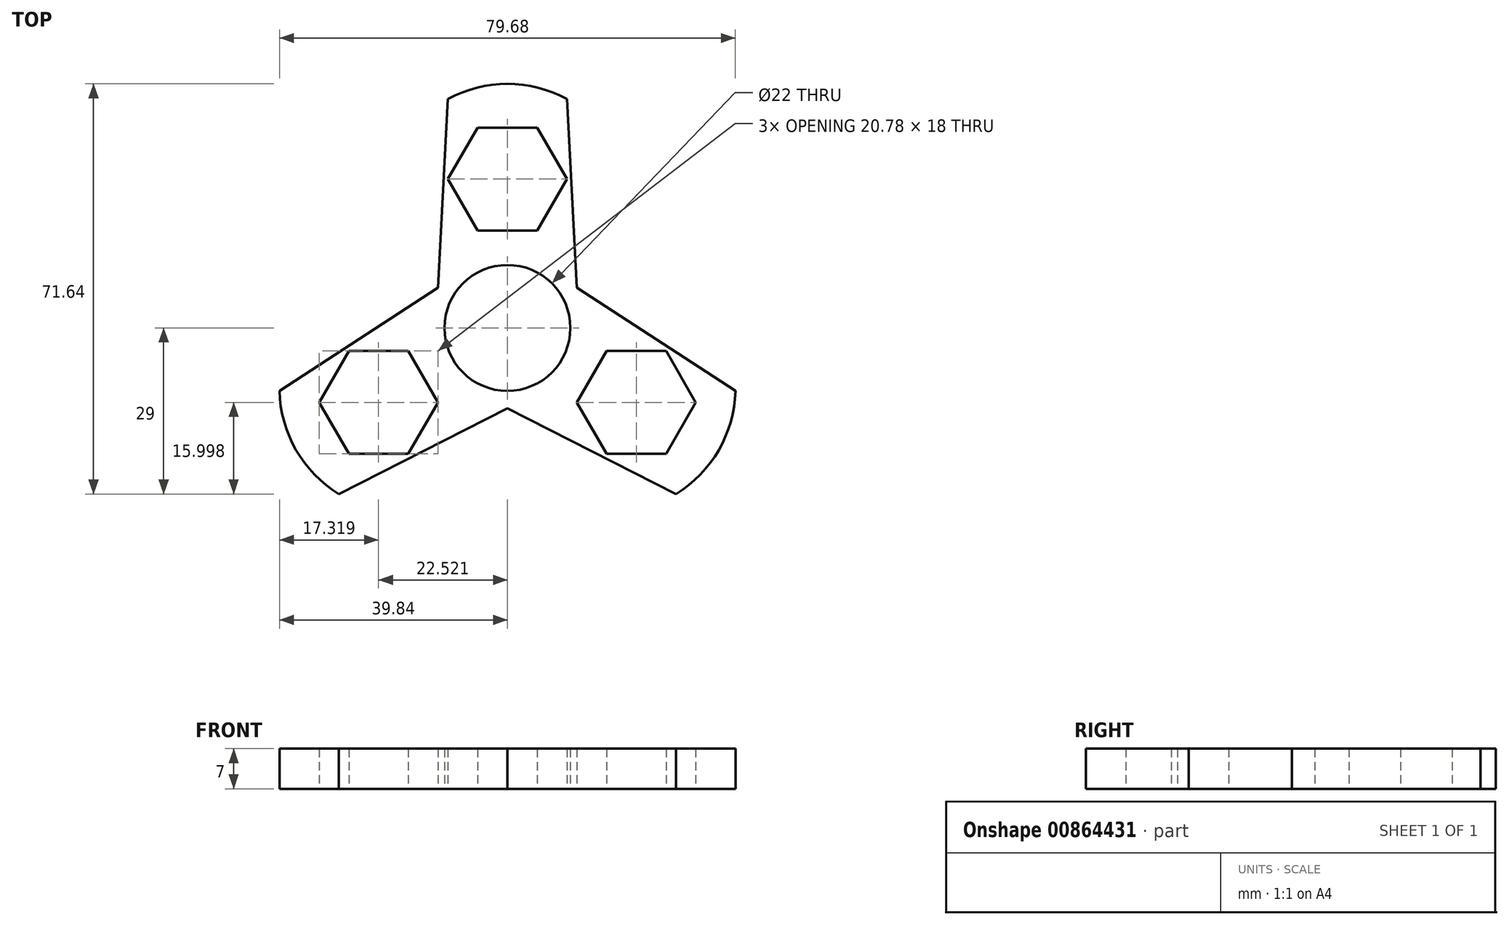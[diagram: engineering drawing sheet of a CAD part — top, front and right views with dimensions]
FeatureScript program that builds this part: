
annotation { "Feature Type Name" : "Feature", "Feature Type Description" : "" }
export const myFeature = defineFeature(function(context is Context, id is Id, definition is map)
    precondition{}
    {
        {
            var Q0;
            Q0=qCreatedBy(makeId("Top.planeOp"),FACE);
            var sketch = newSketch(context, id + "F0", { "sketchPlane" : qUnion([Q0])});
            skCircle(sketch, "E0", {"center": v(0, 0) * mm, "radius": 11 * mm});
            skCircle(sketch, "E1.0", {"center": v(0, 0) * mm, "radius": 14 * mm});
            skCircle(sketch, "E2", {"center": v(0, 0) * mm, "radius": 45 * mm, "construction": true});
            skLineSegment(sketch, "E3", {"start": v(-7.68, 21.31) * mm, "end": v(-7.68, 21.32) * mm});
            skLineSegment(sketch, "E4.MirrorCS", {"start": v(7.68, 21.31) * mm, "end": v(7.68, 21.32) * mm});
            skCircle(sketch, "E5.cCircle", {"center": v(0, 26) * mm, "radius": 9 * mm, "construction": true});
            skPoint(sketch, "E5.cCircle.centerSnap0", {"position": v(6.74, 26) * mm});
            skLineSegment(sketch, "E5.0", {"start": v(-5.2, 35) * mm, "end": v(5.2, 35) * mm});
            skLineSegment(sketch, "E5.1", {"start": v(5.2, 35) * mm, "end": v(10.4, 26) * mm});
            skLineSegment(sketch, "E5.2", {"start": v(10.4, 26) * mm, "end": v(5.2, 17) * mm});
            skLineSegment(sketch, "E5.3", {"start": v(5.2, 17) * mm, "end": v(-5.2, 17) * mm});
            skLineSegment(sketch, "E5.4", {"start": v(-5.2, 17) * mm, "end": v(-10.4, 26) * mm});
            skLineSegment(sketch, "E5.5", {"start": v(-10.4, 26) * mm, "end": v(-5.2, 35) * mm});
            skPoint(sketch, "E5.0.midPoint", {"position": v(0, 35) * mm});
            skLineSegment(sketch, "E6.trimOffspring", {"start": v(-5.28, 33.3) * mm, "end": v(-4.93, 35) * mm});
            skLineSegment(sketch, "E7.trimOffspring", {"start": v(5.28, 33.3) * mm, "end": v(4.93, 35) * mm});
            skPoint(sketch, "E8.start.orphan", {"position": v(-3.48, 42.2) * mm});
            skPoint(sketch, "E9.orphan", {"position": v(-10, 9.8) * mm});
            skPoint(sketch, "E10.orphan", {"position": v(10, 9.8) * mm});
            skPoint(sketch, "E11.orphan", {"position": v(3.48, 42.2) * mm});
            skPoint(sketch, "E12.end.orphan", {"position": v(-10.4, 40) * mm});
            skLineSegment(sketch, "E13", {"start": v(-12.15, 6.96) * mm, "end": v(-10.4, 40) * mm});
            skLineSegment(sketch, "E14.MirrorCS", {"start": v(12.15, 6.96) * mm, "end": v(10.4, 40) * mm});
            skArc(sketch, "E15", {"start": v(10.4, 40) * mm, "mid": v(0, 42.64) * mm, "end": v(-10.4, 40) * mm});
            skCircle(sketch, "E16.1.0", {"center": v(-22.52, -13) * mm, "radius": 9 * mm, "construction": true});
            skArc(sketch, "E16.1.1", {"start": v(-39.84, -11) * mm, "mid": v(-36.93, -21.32) * mm, "end": v(-29.45, -29) * mm});
            skLineSegment(sketch, "E16.1.2", {"start": v(0.04, -14) * mm, "end": v(-29.45, -29) * mm});
            skLineSegment(sketch, "E16.1.3", {"start": v(-12.1, 7.04) * mm, "end": v(-39.84, -11) * mm});
            skLineSegment(sketch, "E16.1.4", {"start": v(-17.32, -22) * mm, "end": v(-27.72, -22) * mm});
            skLineSegment(sketch, "E16.1.5", {"start": v(-12.13, -13) * mm, "end": v(-17.32, -22) * mm});
            skLineSegment(sketch, "E16.1.6", {"start": v(-17.32, -4) * mm, "end": v(-12.13, -13) * mm});
            skLineSegment(sketch, "E16.1.7", {"start": v(-27.72, -4) * mm, "end": v(-17.32, -4) * mm});
            skLineSegment(sketch, "E16.1.8", {"start": v(-32.91, -13) * mm, "end": v(-27.72, -4) * mm});
            skLineSegment(sketch, "E16.1.9", {"start": v(-27.72, -22) * mm, "end": v(-32.91, -13) * mm});
            skCircle(sketch, "E16.2.0", {"center": v(22.52, -13) * mm, "radius": 9 * mm, "construction": true});
            skArc(sketch, "E16.2.1", {"start": v(29.45, -29) * mm, "mid": v(36.93, -21.32) * mm, "end": v(39.84, -11) * mm});
            skLineSegment(sketch, "E16.2.2", {"start": v(12.1, 7.04) * mm, "end": v(39.84, -11) * mm});
            skLineSegment(sketch, "E16.2.3", {"start": v(-0.04, -14) * mm, "end": v(29.45, -29) * mm});
            skLineSegment(sketch, "E16.2.4", {"start": v(27.72, -4) * mm, "end": v(32.91, -13) * mm});
            skLineSegment(sketch, "E16.2.5", {"start": v(17.32, -4) * mm, "end": v(27.72, -4) * mm});
            skLineSegment(sketch, "E16.2.6", {"start": v(12.13, -13) * mm, "end": v(17.32, -4) * mm});
            skLineSegment(sketch, "E16.2.7", {"start": v(17.32, -22) * mm, "end": v(12.13, -13) * mm});
            skLineSegment(sketch, "E16.2.8", {"start": v(27.72, -22) * mm, "end": v(17.32, -22) * mm});
            skLineSegment(sketch, "E16.2.9", {"start": v(32.91, -13) * mm, "end": v(27.72, -22) * mm});
            skSolve(sketch);
        }
        {
            var Q0;
            Q0=qSketchRegion(id+"F0",true);
            var Q1;
            Q1=makeQuery(id+"F0.imprint","IMPRINT",FACE,{"disambiguationData":[TD([[makeQuery(id+"F0.imprint","IMPRINT",EDGE,{"derivedFrom":sQuery(id+"F0.wireOp",EDGE,"E0")}),-1.0]])]});
            extrude(context, id + "F1", {"entities" : qUnion([Q0, Q1]), "depth" : 7 * mm, "offsetDistance" : 25 * mm});
        }
    });
